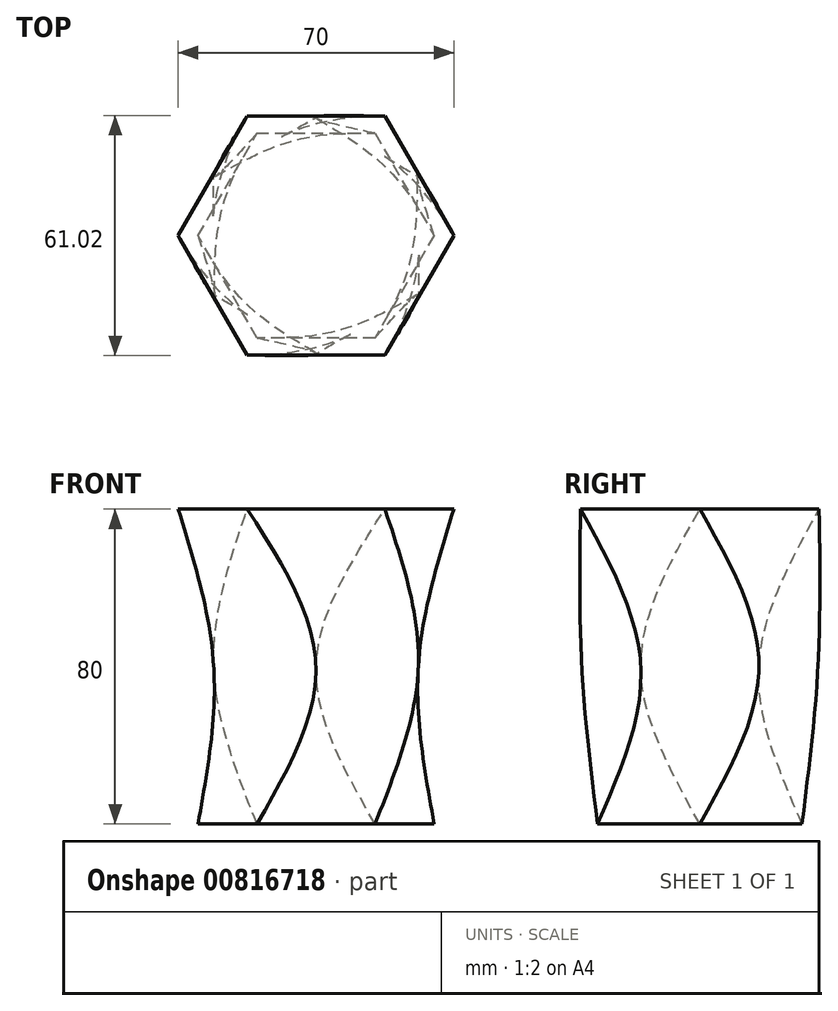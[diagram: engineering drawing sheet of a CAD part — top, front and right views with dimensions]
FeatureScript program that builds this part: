
annotation { "Feature Type Name" : "Feature", "Feature Type Description" : "" }
export const myFeature = defineFeature(function(context is Context, id is Id, definition is map)
    precondition{}
    {
        {
            var Q0;
            Q0=qCreatedBy(makeId("Top.planeOp"),FACE);
            var sketch = newSketch(context, id + "F0", { "sketchPlane" : qUnion([Q0])});
            skCircle(sketch, "E0.cCircle", {"center": v(0, 0) * mm, "radius": 30 * mm, "construction": true});
            skLineSegment(sketch, "E0.0", {"start": v(30, 0) * mm, "end": v(15, -25.98) * mm});
            skLineSegment(sketch, "E0.1", {"start": v(15, -25.98) * mm, "end": v(-15, -25.98) * mm});
            skLineSegment(sketch, "E0.2", {"start": v(-15, -25.98) * mm, "end": v(-30, 0) * mm});
            skLineSegment(sketch, "E0.3", {"start": v(-30, 0) * mm, "end": v(-15, 25.98) * mm});
            skLineSegment(sketch, "E0.4", {"start": v(-15, 25.98) * mm, "end": v(15, 25.98) * mm});
            skLineSegment(sketch, "E0.5", {"start": v(15, 25.98) * mm, "end": v(30, 0) * mm});
            skSolve(sketch);
        }
        {
            var Q0;
            Q0=qCreatedBy(makeId("Top.planeOp"),FACE);
            cPlane(context, id + "F1", {"entities" : qUnion([Q0]), "cplaneType" : CPlaneType.OFFSET, "offset" : 40 * mm, "width" : 150 * mm, "height" : 150 * mm});
        }
        {
            var Q0;
            Q0=qCreatedBy(id+"F1.planeOp",FACE);
            var sketch = newSketch(context, id + "F2", { "sketchPlane" : qUnion([Q0])});
            skCircle(sketch, "E1.cCircle", {"center": v(0, 0) * mm, "radius": 30 * mm, "construction": true});
            skLineSegment(sketch, "E1.0", {"start": v(25.98, 15) * mm, "end": v(25.98, -15) * mm});
            skLineSegment(sketch, "E1.1", {"start": v(25.98, -15) * mm, "end": v(0, -30) * mm});
            skLineSegment(sketch, "E1.2", {"start": v(0, -30) * mm, "end": v(-25.98, -15) * mm});
            skLineSegment(sketch, "E1.3", {"start": v(-25.98, -15) * mm, "end": v(-25.98, 15) * mm});
            skLineSegment(sketch, "E1.4", {"start": v(-25.98, 15) * mm, "end": v(0, 30) * mm});
            skLineSegment(sketch, "E1.5", {"start": v(0, 30) * mm, "end": v(25.98, 15) * mm});
            skSolve(sketch);
        }
        {
            var Q0;
            Q0=qCreatedBy(id+"F1.planeOp",FACE);
            cPlane(context, id + "F3", {"entities" : qUnion([Q0]), "cplaneType" : CPlaneType.OFFSET, "offset" : 40 * mm, "width" : 150 * mm, "height" : 150 * mm});
        }
        {
            var Q0;
            Q0=qCreatedBy(id+"F3.planeOp",FACE);
            var sketch = newSketch(context, id + "F4", { "sketchPlane" : qUnion([Q0])});
            skCircle(sketch, "E2.cCircle", {"center": v(0, 0) * mm, "radius": 35 * mm, "construction": true});
            skLineSegment(sketch, "E2.0", {"start": v(17.5, 30.31) * mm, "end": v(35, 0) * mm});
            skLineSegment(sketch, "E2.1", {"start": v(35, 0) * mm, "end": v(17.5, -30.31) * mm});
            skLineSegment(sketch, "E2.2", {"start": v(17.5, -30.31) * mm, "end": v(-17.5, -30.31) * mm});
            skLineSegment(sketch, "E2.3", {"start": v(-17.5, -30.31) * mm, "end": v(-35, 0) * mm});
            skLineSegment(sketch, "E2.4", {"start": v(-35, 0) * mm, "end": v(-17.5, 30.31) * mm});
            skLineSegment(sketch, "E2.5", {"start": v(-17.5, 30.31) * mm, "end": v(17.5, 30.31) * mm});
            skSolve(sketch);
        }
        {
            var Q0;
            Q0=makeQuery(id+"F0.imprint","IMPRINT",FACE,{"disambiguationData":[TD([[makeQuery(id+"F0.imprint","IMPRINT",EDGE,{"derivedFrom":sQuery(id+"F0.wireOp",EDGE,"E0.0")}),-1.0]])]});
            var Q1;
            Q1=makeQuery(id+"F2.imprint","IMPRINT",FACE,{"disambiguationData":[TD([[makeQuery(id+"F2.imprint","IMPRINT",EDGE,{"derivedFrom":sQuery(id+"F2.wireOp",EDGE,"E1.0")}),-1.0]])]});
            var Q2;
            Q2=makeQuery(id+"F4.imprint","IMPRINT",FACE,{"disambiguationData":[TD([[makeQuery(id+"F4.imprint","IMPRINT",EDGE,{"derivedFrom":sQuery(id+"F4.wireOp",EDGE,"E2.0")}),-1.0]])]});
            loft(context, id + "F5", {"sheetProfilesArray" : [{ "sheetProfileEntities" : qUnion([Q0]) }, { "sheetProfileEntities" : qUnion([Q1]) }, { "sheetProfileEntities" : qUnion([Q2]) }]});
        }
    });
